# Revit family: 359745
name_source: partatom
category: Plumbing Fixtures
revit_build: Autodesk Revit 2013 (Build: 20120221_2030(x64)
units: mm (PartAtom-declared; Revit-internal decimal feet)

## types (1)
- 359745
    Assembly Code = D2090800
    CW Connection = Yes
    Calculation flow rate = 0.10 l/s
    Flow time = 1-15 adjustable
    HW Connection = Yes
    Manufacturer = FRANKE KITCHEN SYSTEMS (PTY) LTD
    Material = Chromium-plated Brass, Polished
    Minimum flow pressure = 1.0 Bar
    Model = Aqualine-C AQUA203 Self-Closing Piller Tap
    Product Code = 359745
    Sound insulation = Noise group I
    Specification = Noise group I, for wash systems, with aerator with intergrated flow controller, Optionally for connecting to cold water or pre-mixed warm water, Self-closing functional cartridge, piston-free design, with automatic and backlash free closure. Adjustable flow duration. Full metal construction with twist-proof operating element, polished chromium-plated brass.
    Vent Connection = No
    Volumetric flow = 0.10 l/s at a flow pressure of 3 bar
    Waste Connection = No

## geometry (parser evidence)
native form markers: Blend x4, Sweep x1
no freeform markers — native parametric forms only
